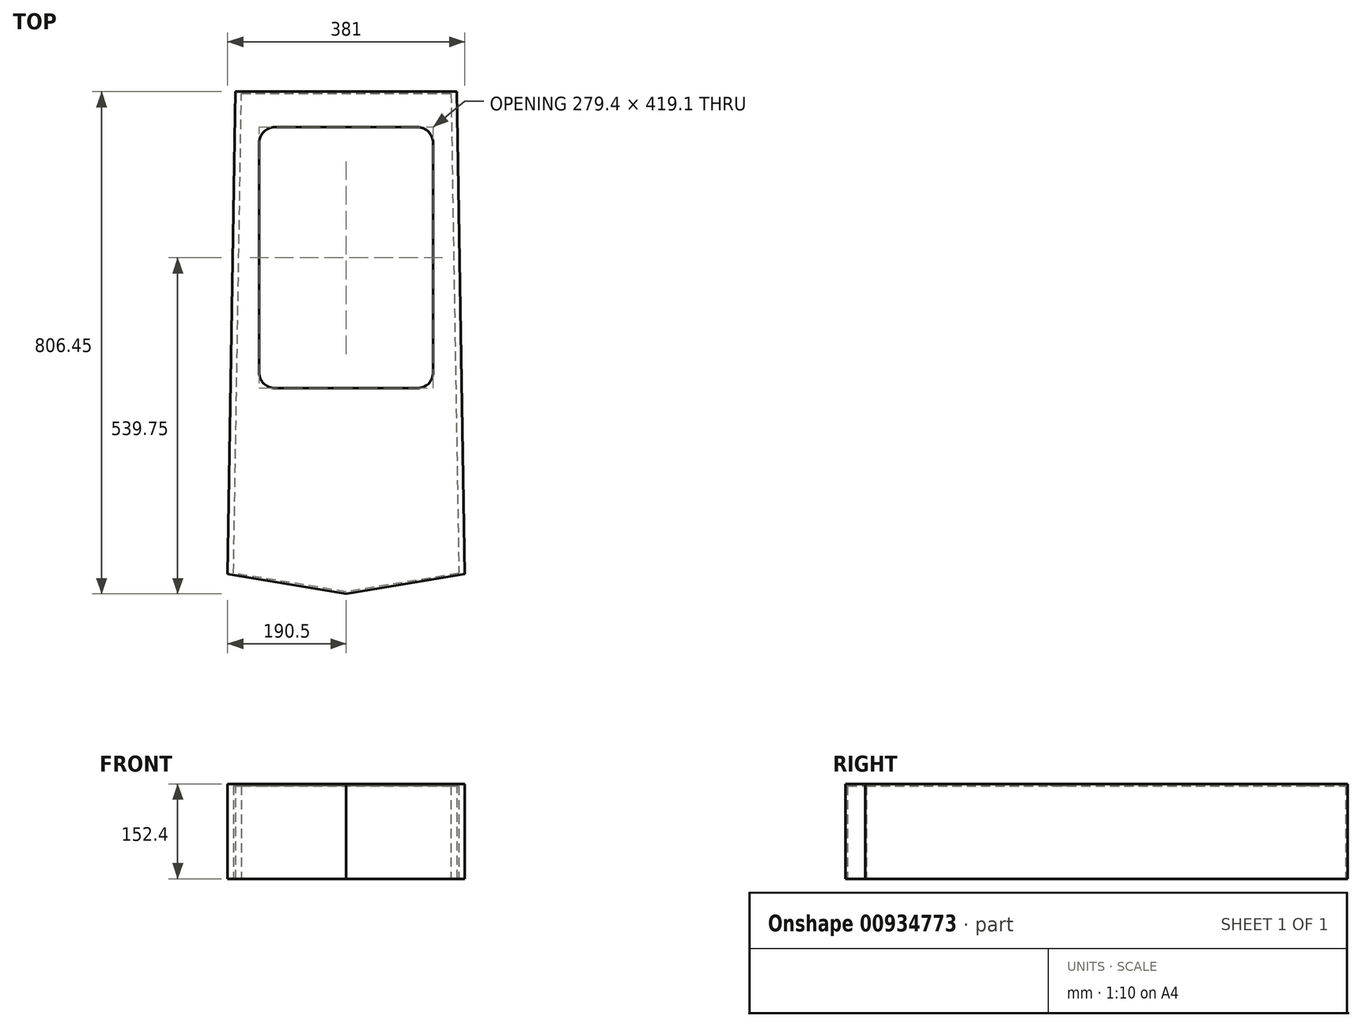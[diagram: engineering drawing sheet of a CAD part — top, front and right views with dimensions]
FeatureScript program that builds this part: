
annotation { "Feature Type Name" : "Feature", "Feature Type Description" : "" }
export const myFeature = defineFeature(function(context is Context, id is Id, definition is map)
    precondition{}
    {
        {
            var Q0;
            Q0=qCreatedBy(makeId("Top.planeOp"),FACE);
            var sketch = newSketch(context, id + "F0", { "sketchPlane" : qUnion([Q0])});
            skLineSegment(sketch, "E0", {"start": v(-190.5, 0) * mm, "end": v(190.5, 0) * mm});
            skLineSegment(sketch, "E1", {"start": v(190.5, 0) * mm, "end": v(177.8, 774.7) * mm});
            skLineSegment(sketch, "E2", {"start": v(177.8, 774.7) * mm, "end": v(-177.8, 774.7) * mm});
            skLineSegment(sketch, "E3", {"start": v(-177.8, 774.7) * mm, "end": v(-190.5, 0) * mm});
            skLineSegment(sketch, "E4", {"start": v(-190.5, 0) * mm, "end": v(0, -31.75) * mm});
            skLineSegment(sketch, "E5", {"start": v(0, -31.75) * mm, "end": v(190.5, 0) * mm});
            skSolve(sketch);
        }
        {
            var Q0;
            Q0 = qSketchRegion(id + "F0", true);
            extrude(context, id + "F1", {"entities" : qUnion([Q0]), "depth" : 152.4 * mm, "offsetDistance" : 25.4 * mm});
        }
        {
            var Q0;
            Q0=makeQuery(id+"F1.opExtrude","CAP_FACE",FACE,{"disambiguationData":[OSD([sQuery(id+"F0.wireOp",EDGE,"E1"),sQuery(id+"F0.wireOp",EDGE,"E2"),sQuery(id+"F0.wireOp",EDGE,"E3"),sQuery(id+"F0.wireOp",EDGE,"E4"),sQuery(id+"F0.wireOp",EDGE,"E5")])],"isStart":true});
            var sketch = newSketch(context, id + "F2", { "sketchPlane" : qUnion([Q0])});
            skLineSegment(sketch, "E6", {"start": v(-180.95, -1.63) * mm, "end": v(-168.33, -771.53) * mm});
            skLineSegment(sketch, "E7", {"start": v(-168.33, -771.53) * mm, "end": v(168.33, -771.53) * mm});
            skLineSegment(sketch, "E8", {"start": v(168.33, -771.53) * mm, "end": v(180.95, -1.63) * mm});
            skLineSegment(sketch, "E9", {"start": v(180.95, -1.63) * mm, "end": v(0, 28.53) * mm});
            skLineSegment(sketch, "E10", {"start": v(0, 28.53) * mm, "end": v(-180.95, -1.63) * mm});
            skSolve(sketch);
        }
        {
            var Q0;
            Q0 = qSketchRegion(id + "F2", true);
            extrude(context, id + "F3", {"entities" : qUnion([Q0]), "operationType" : NewBodyOperationType.REMOVE, "oppositeDirection" : true, "depth" : 149.22 * mm, "offsetDistance" : 25.4 * mm});
        }
        {
            var Q0;
            Q0=makeQuery(id+"F1.opExtrude","CAP_FACE",FACE,{"disambiguationData":[OSD([sQuery(id+"F0.wireOp",EDGE,"E1"),sQuery(id+"F0.wireOp",EDGE,"E2"),sQuery(id+"F0.wireOp",EDGE,"E3"),sQuery(id+"F0.wireOp",EDGE,"E4"),sQuery(id+"F0.wireOp",EDGE,"E5")])],"isStart":false});
            var Q1;
            Q1=makeQuery(id+"F1.opExtrude","CAP_FACE",FACE,{"disambiguationData":[OSD([sQuery(id+"F0.wireOp",EDGE,"E1"),sQuery(id+"F0.wireOp",EDGE,"E2"),sQuery(id+"F0.wireOp",EDGE,"E3"),sQuery(id+"F0.wireOp",EDGE,"E4"),sQuery(id+"F0.wireOp",EDGE,"E5")])],"isStart":false});
            var sketch = newSketch(context, id + "F4", { "sketchPlane" : qUnion([Q0, Q1])});
            skLineSegment(sketch, "E11.bottom", {"start": v(-114.3, 717.55) * mm, "end": v(114.3, 717.55) * mm});
            skLineSegment(sketch, "E11.top", {"start": v(-114.3, 298.45) * mm, "end": v(114.3, 298.45) * mm});
            skLineSegment(sketch, "E11.left", {"start": v(-139.7, 692.15) * mm, "end": v(-139.7, 323.85) * mm});
            skLineSegment(sketch, "E11.right", {"start": v(139.7, 692.15) * mm, "end": v(139.7, 323.85) * mm});
            skPoint(sketch, "E12.visualSharp", {"position": v(-139.7, 717.55) * mm});
            skArc(sketch, "E12.filletArc", {"start": v(-114.3, 717.55) * mm, "mid": v(-132.26, 710.11) * mm, "end": v(-139.7, 692.15) * mm});
            skPoint(sketch, "E13.visualSharp", {"position": v(139.7, 717.55) * mm});
            skArc(sketch, "E13.filletArc", {"start": v(139.7, 692.15) * mm, "mid": v(132.26, 710.11) * mm, "end": v(114.3, 717.55) * mm});
            skPoint(sketch, "E14.visualSharp", {"position": v(139.7, 298.45) * mm});
            skArc(sketch, "E14.filletArc", {"start": v(114.3, 298.45) * mm, "mid": v(132.26, 305.89) * mm, "end": v(139.7, 323.85) * mm});
            skPoint(sketch, "E15.visualSharp", {"position": v(-139.7, 298.45) * mm});
            skArc(sketch, "E15.filletArc", {"start": v(-139.7, 323.85) * mm, "mid": v(-132.26, 305.89) * mm, "end": v(-114.3, 298.45) * mm});
            skSolve(sketch);
        }
        {
            var Q0;
            Q0 = qSketchRegion(id + "F4", true);
            extrude(context, id + "F5", {"entities" : qUnion([Q0]), "operationType" : NewBodyOperationType.REMOVE, "oppositeDirection" : true, "depth" : 25.4 * mm, "offsetDistance" : 25.4 * mm});
        }
    });
